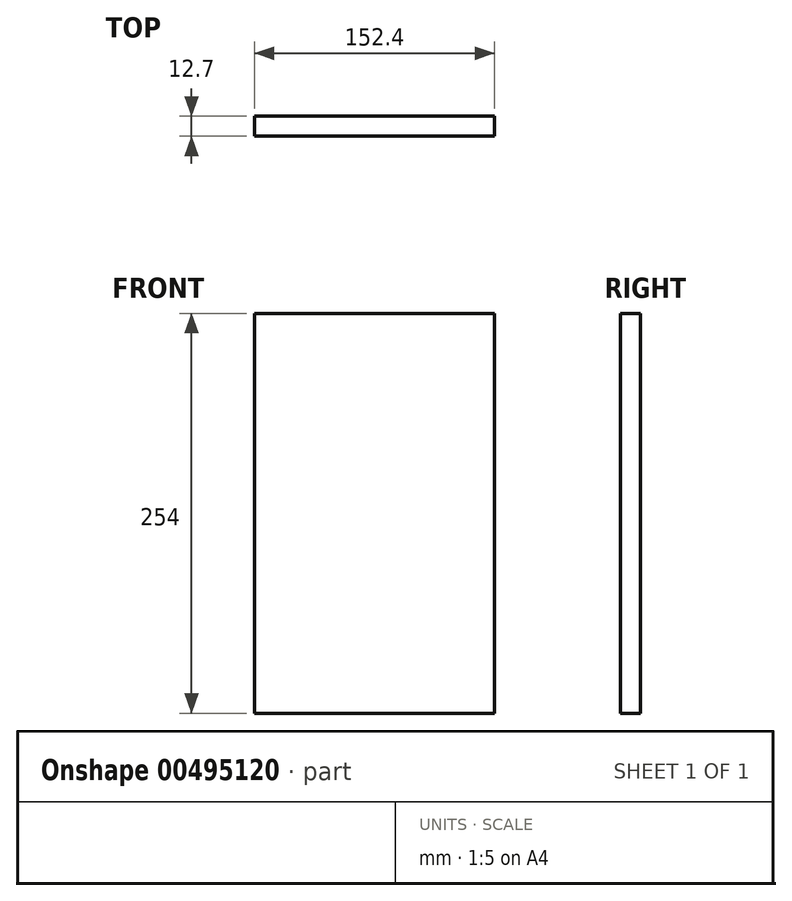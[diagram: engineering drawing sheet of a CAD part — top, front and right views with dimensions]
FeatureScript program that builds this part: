
annotation { "Feature Type Name" : "Feature", "Feature Type Description" : "" }
export const myFeature = defineFeature(function(context is Context, id is Id, definition is map)
    precondition{}
    {
        {
            var Q0;
            Q0=qCreatedBy(makeId("Front.planeOp"),FACE);
            var sketch = newSketch(context, id + "F0", { "sketchPlane" : qUnion([Q0])});
            skLineSegment(sketch, "E0.bottom", {"start": v(0, 0) * mm, "end": v(-152.4, 0) * mm});
            skLineSegment(sketch, "E0.top", {"start": v(0, 254) * mm, "end": v(-152.4, 254) * mm});
            skLineSegment(sketch, "E0.left", {"start": v(0, 0) * mm, "end": v(0, 254) * mm});
            skLineSegment(sketch, "E0.right", {"start": v(-152.4, 0) * mm, "end": v(-152.4, 254) * mm});
            skSolve(sketch);
        }
        {
            var Q0;
            Q0 = qSketchRegion(id + "F0", true);
            extrude(context, id + "F1", {"entities" : qUnion([Q0]), "depth" : 12.7 * mm});
        }
    });
